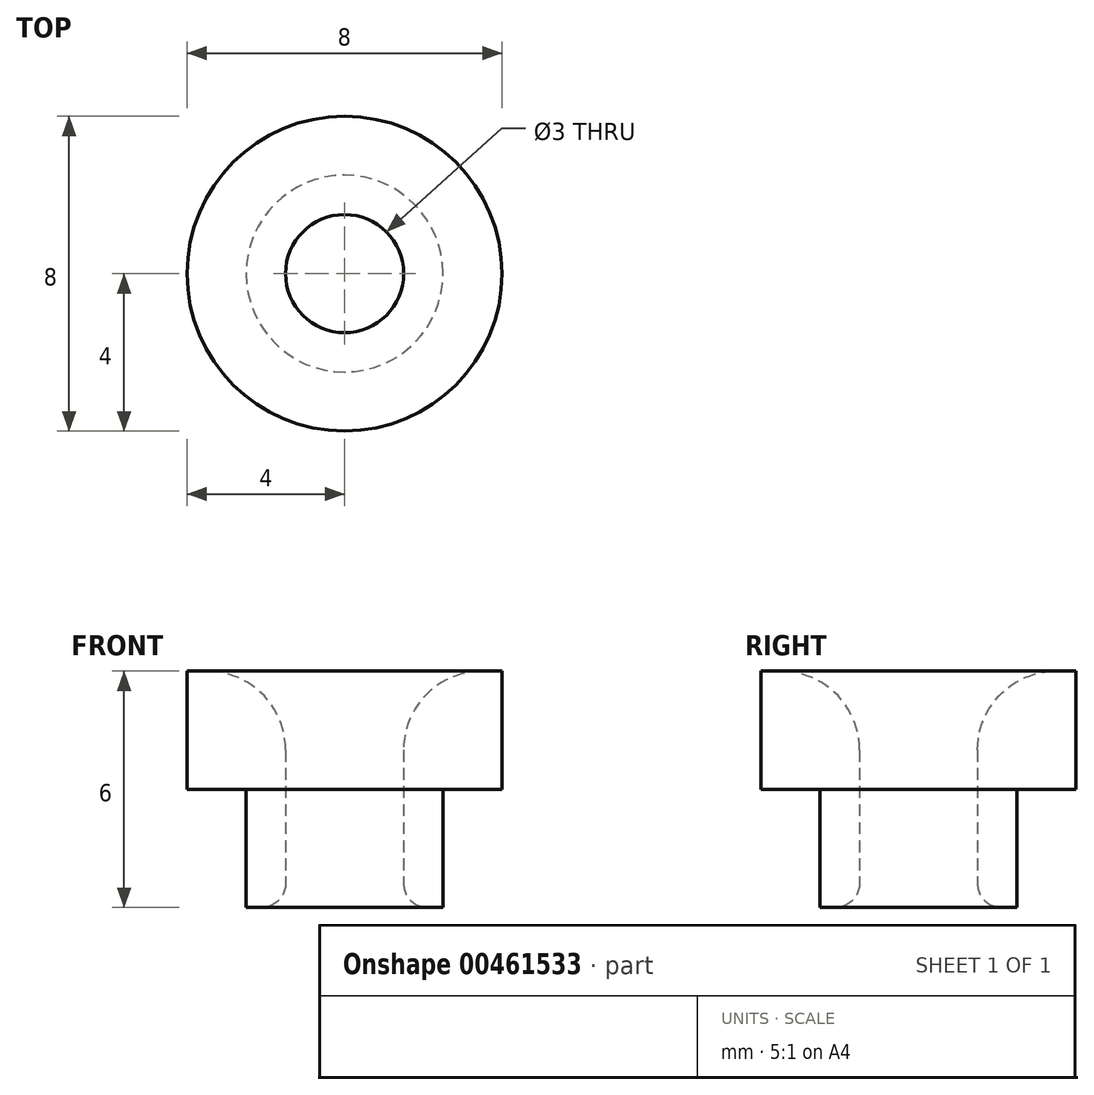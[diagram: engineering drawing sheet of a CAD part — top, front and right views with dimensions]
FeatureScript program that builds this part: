
annotation { "Feature Type Name" : "Feature", "Feature Type Description" : "" }
export const myFeature = defineFeature(function(context is Context, id is Id, definition is map)
    precondition{}
    {
        {
            var Q0;
            Q0=qCreatedBy(makeId("Top.planeOp"),FACE);
            var sketch = newSketch(context, id + "F0", { "sketchPlane" : qUnion([Q0])});
            skCircle(sketch, "E0", {"center": v(0, 0) * mm, "radius": 4 * mm});
            skCircle(sketch, "E1", {"center": v(0, 0) * mm, "radius": 1.5 * mm});
            skCircle(sketch, "E2", {"center": v(0, 0) * mm, "radius": 2.5 * mm});
            skSolve(sketch);
        }
        {
            var Q0;
            Q0 = qSketchRegion(id + "F0", true);
            var Q1;
            Q1=makeQuery(id+"F0.imprint","IMPRINT",FACE,{"disambiguationData":[TD([[makeQuery(id+"F0.imprint","IMPRINT",EDGE,{"derivedFrom":sQuery(id+"F0.wireOp",EDGE,"E1")}),-1.0]])]});
            extrude(context, id + "F1", {"entities" : qUnion([Q0, Q1]), "depth" : 3 * mm});
        }
        {
            var Q0;
            Q0=makeQuery(id+"F0.imprint","IMPRINT",FACE,{"disambiguationData":[TD([[makeQuery(id+"F0.imprint","IMPRINT",EDGE,{"derivedFrom":sQuery(id+"F0.wireOp",EDGE,"E1")}),-1.0]])]});
            extrude(context, id + "F2", {"entities" : qUnion([Q0]), "operationType" : NewBodyOperationType.ADD, "depth" : -3 * mm});
        }
        {
            var Q0;
            Q0=makeQuery(id+"F2.opExtrude","CAP_EDGE",EDGE,{"disambiguationData":[OSD([sQuery(id+"F0.wireOp",EDGE,"E1")])],"isStart":false});
            fillet(context, id + "F3", {"entities" : qUnion([Q0]), "radius" : 0.6 * mm, "tangentPropagation" : true, "allowEdgeOverflow" : false});
        }
        {
            var Q0;
            Q0=makeQuery(id+"F1.opExtrude","CAP_EDGE",EDGE,{"disambiguationData":[OSD([sQuery(id+"F0.wireOp",EDGE,"E1")])],"isStart":false});
            fillet(context, id + "F4", {"entities" : qUnion([Q0]), "radius" : 2 * mm, "tangentPropagation" : true, "allowEdgeOverflow" : false});
        }
    });
